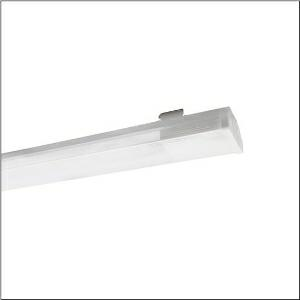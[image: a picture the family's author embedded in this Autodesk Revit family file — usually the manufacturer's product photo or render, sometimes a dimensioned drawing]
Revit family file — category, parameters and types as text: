
# Revit family: modario_r__31_gen_2_53bm8127u4m1d2_fd66
name_source: partatom
category: Lighting Fixtures
units: mm (PartAtom-declared; Revit-internal decimal feet)

## family parameters
Cut with Voids When Loaded = No
Host = Face
Light Source = No
Part Type = Normal
Room Calculation Point = No
Round Connector Dimension = Use Diameter
Shared = No

## types (1)
- Modario® 31 Gen.2 (1 x LED, 26560 lm, 143.7 W, 4000K)
    Apparent Load = 144 VA
    CIE Flux Codes = 47 80 95 93 100
    Color Rendering = 80
    Color Temperature = 4000K
    Default Elevation = 1800 mm
    Description = Modario® 31 Gen.2, luminaire insert, of sheet steel, coil coated, white, length: 2.392mm, width: 81mm, height: 82mm, 8x system unit, system units: 299mm, LED rated luminous flux: 26.560lm, light colour: 840, control gear: ON/OFF, with plug, 3-pole, with phase selection, mains connection: 220..240V, AC, 50/60Hz, rated input power: 144W, through-wiring accessed according to module size, primary optical cover: cover, of PMMA, light emission: direct distribution, primary light characteristic: symmetric, protection rating (complete): IP20, protection rating (LED compartment): IP50, insulation class (complete): insulation class I (protective earthing), certification: CE, ENEC, VDE, UKCA, impact resistance: IK03, permissible ambient temperature for indoor applications: -40..+30°C, corresponds to IFS (International Featured Standards) requirements for safety and quality in the food industry, reducing of maximum allowable ambient temperature of 5°C with ceiling mounting, packaging unit: 1 piece
    Height = 92 mm
    Lamp = 1 x LED
    Lamp Light Flux = 26560 lm
    Lamp Power = 143.7 W
    Lamp count = 1
    Length = 2392 mm
    Luminous efficacy = 185 lm/W
    Manufacturer = Siteco
    ModVariant = No
    Model = 53BM8127U4M1D2
    Mounting Place = Ceiling
    Mounting Type = Pendant
    Number of Poles = 1
    OnlyDefault = Yes
    Power Factor = 1
    Product Name = Modario® 31 Gen.2
    Product group = luminaire insert
    ProductGroupID = 902
    Protection Class = Protection class I
    Protection Degree = IP 20
    RLX_Detail_Level = 1
    RLX_Emergency_Light_Flux = 0 lm
    RLX_Emergency_Type = 0
    RLX_Emergency_Type_DB = No
    RlxData = <blob elided: 34537 chars, md5=3a0eaf2d>
    Socket = socket
    Standby Power = 0 W
    System Light Flux = 26560 lm
    System Power = 144 W
    Type Comments = Product without accessories
    Type Image = l_1341883.jpg
    URL = http://relux.com
    VarID = ---
    Voltage = 0 V
    Weight = 0.00 kg
    Width = 81 mm

## geometry (parser evidence)
native form markers: Blend x4, Sweep x13
no freeform markers — native parametric forms only
